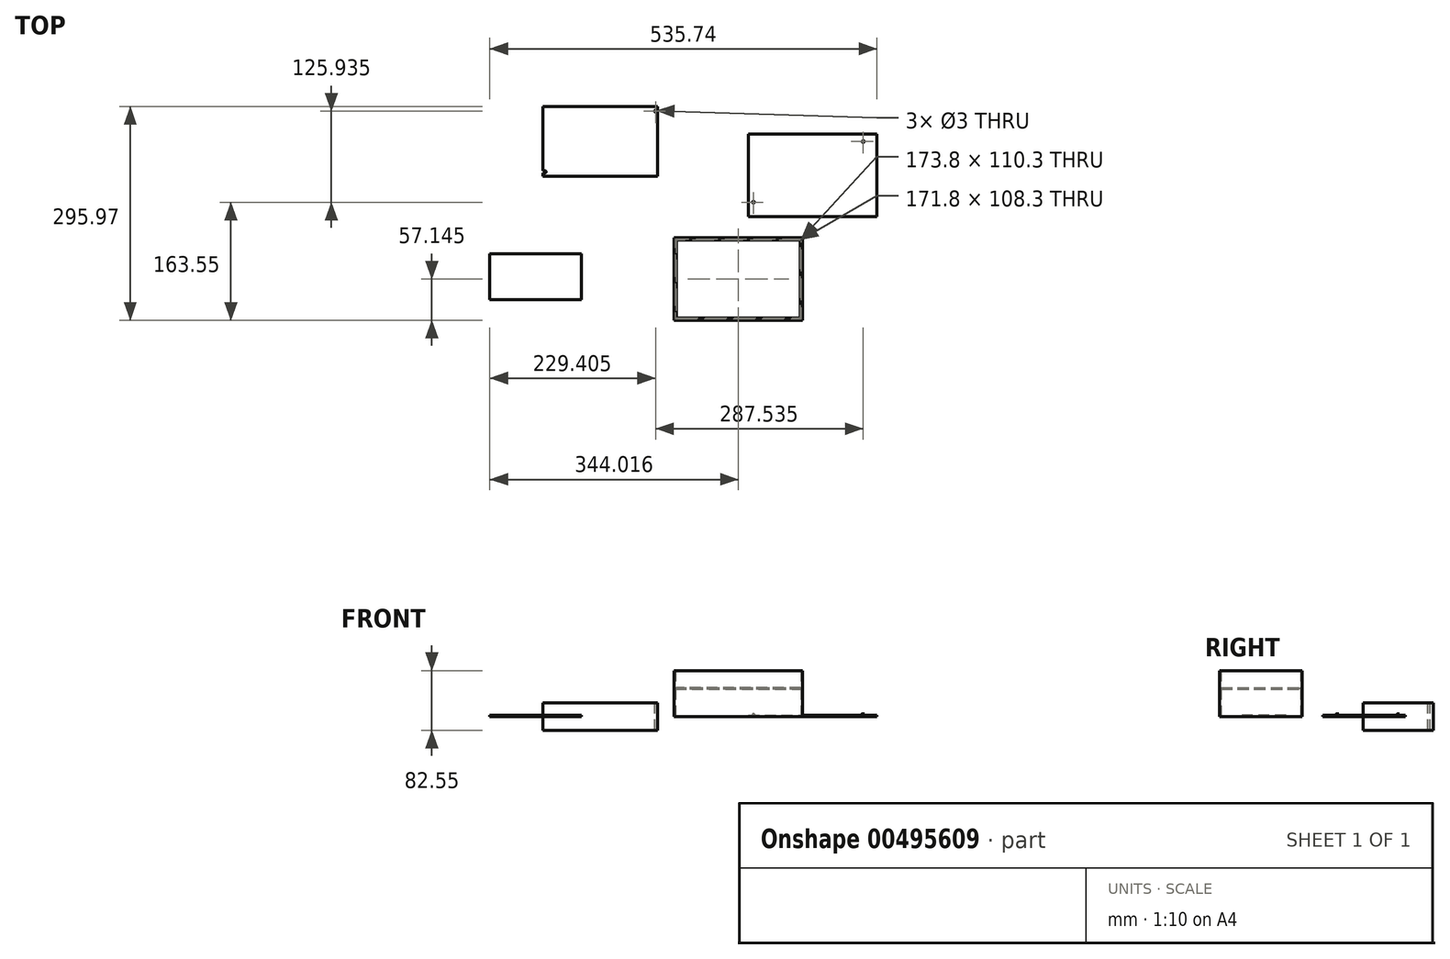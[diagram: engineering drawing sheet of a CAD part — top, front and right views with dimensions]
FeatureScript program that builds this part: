
annotation { "Feature Type Name" : "Feature", "Feature Type Description" : "" }
export const myFeature = defineFeature(function(context is Context, id is Id, definition is map)
    precondition{}
    {
        {
            var Q0;
            Q0=qCreatedBy(makeId("Top.planeOp"),FACE);
            var sketch = newSketch(context, id + "F0", { "sketchPlane" : qUnion([Q0])});
            skLineSegment(sketch, "E0.bottom", {"start": v(79.38, -48.42) * mm, "end": v(-79.38, -48.42) * mm});
            skLineSegment(sketch, "E0.top", {"start": v(79.38, 48.42) * mm, "end": v(-79.38, 48.42) * mm});
            skLineSegment(sketch, "E0.left", {"start": v(79.38, -48.42) * mm, "end": v(79.38, 48.42) * mm});
            skLineSegment(sketch, "E0.right", {"start": v(-79.38, -48.42) * mm, "end": v(-79.38, 48.42) * mm});
            skPoint(sketch, "E0.middle", {"position": v(0, 0) * mm});
            skLineSegment(sketch, "E1.bottom", {"start": v(-79.38, -43.42) * mm, "end": v(-73.38, -43.42) * mm});
            skLineSegment(sketch, "E1.top", {"start": v(-79.38, -40.42) * mm, "end": v(-73.38, -40.42) * mm});
            skLineSegment(sketch, "E1.left", {"start": v(-79.38, -43.42) * mm, "end": v(-79.38, -40.42) * mm});
            skLineSegment(sketch, "E1.right", {"start": v(-73.38, -43.42) * mm, "end": v(-73.38, -40.42) * mm});
            skLineSegment(sketch, "E2.bottom", {"start": v(79.38, 43.42) * mm, "end": v(73.38, 43.42) * mm});
            skLineSegment(sketch, "E2.top", {"start": v(79.38, 40.42) * mm, "end": v(73.38, 40.42) * mm});
            skLineSegment(sketch, "E2.left", {"start": v(79.38, 43.42) * mm, "end": v(79.38, 40.42) * mm});
            skLineSegment(sketch, "E2.right", {"start": v(73.38, 43.42) * mm, "end": v(73.38, 40.42) * mm});
            skCircle(sketch, "E3", {"center": v(76.38, 41.93) * mm, "radius": 1.5 * mm});
            skCircle(sketch, "E4", {"center": v(-76.38, -41.92) * mm, "radius": 1.5 * mm});
            skPoint(sketch, "E4.centerSnap0", {"position": v(-76.38, -40.42) * mm});
            skSolve(sketch);
        }
        {
            var Q0;
            {var subQ6=sQuery(id+"F0.wireOp",EDGE,"E0.bottom");Q0=makeQuery(id+"F0.imprint","IMPRINT",FACE,{"disambiguationData":[TD([[makeQuery(id+"F0.imprint","IMPRINT",EDGE,{"derivedFrom":subQ6}),-1.0]])]});}
            var Q1;
            {var subQ0=sQuery(id+"F0.wireOp",EDGE,"E1.right");Q1=makeQuery(id+"F0.imprint","IMPRINT",FACE,{"disambiguationData":[TD([[makeQuery(id+"F0.imprint","IMPRINT",EDGE,{"derivedFrom":subQ0}),1.0]])]});}
            var Q2;
            {var subQ0=sQuery(id+"F0.wireOp",EDGE,"E1.left");Q2=makeQuery(id+"F0.imprint","IMPRINT",FACE,{"disambiguationData":[TD([[makeQuery(id+"F0.imprint","IMPRINT",EDGE,{"derivedFrom":subQ0}),-1.0]])]});}
            var Q3;
            Q3=makeQuery(id+"F0.imprint","IMPRINT",FACE,{"disambiguationData":[TD([[makeQuery(id+"F0.imprint","IMPRINT",EDGE,{"derivedFrom":sQuery(id+"F0.wireOp",EDGE,"E2.top")}),-1.0]])]});
            extrude(context, id + "F1", {"entities" : qUnion([Q0, Q1, Q2, Q3]), "endBound" : BoundingType.SYMMETRIC, "depth" : 38.1 * mm});
        }
        {
            var Q0;
            Q0=qCreatedBy(makeId("Top.planeOp"),FACE);
            var sketch = newSketch(context, id + "F2", { "sketchPlane" : qUnion([Q0])});
            skLineSegment(sketch, "E5.bottom", {"start": v(204.91, 10) * mm, "end": v(382.71, 10) * mm});
            skLineSegment(sketch, "E5.top", {"start": v(204.91, -104.3) * mm, "end": v(382.71, -104.3) * mm});
            skLineSegment(sketch, "E5.left", {"start": v(204.91, 10) * mm, "end": v(204.91, -104.3) * mm});
            skLineSegment(sketch, "E5.right", {"start": v(382.71, 10) * mm, "end": v(382.71, -104.3) * mm});
            skCircle(sketch, "E6", {"center": v(363.91, 0) * mm, "radius": 1.5 * mm});
            skCircle(sketch, "E7", {"center": v(211.91, -84) * mm, "radius": 1.5 * mm});
            skSolve(sketch);
        }
        {
            var Q0;
            Q0=makeQuery(id+"F2.imprint","IMPRINT",FACE,{"disambiguationData":[TD([[makeQuery(id+"F2.imprint","IMPRINT",EDGE,{"derivedFrom":sQuery(id+"F2.wireOp",EDGE,"E7")}),1.0]])]});
            var Q1;
            Q1=makeQuery(id+"F2.imprint","IMPRINT",FACE,{"disambiguationData":[TD([[makeQuery(id+"F2.imprint","IMPRINT",EDGE,{"derivedFrom":sQuery(id+"F2.wireOp",EDGE,"E6")}),1.0]])]});
            extrude(context, id + "F3", {"entities" : qUnion([Q0, Q1]), "depth" : 4 * mm});
        }
        {
            var Q0;
            Q0=makeQuery(id+"F2.imprint","IMPRINT",FACE,{"disambiguationData":[TD([[makeQuery(id+"F2.imprint","IMPRINT",EDGE,{"derivedFrom":sQuery(id+"F2.wireOp",EDGE,"E5.bottom")}),-1.0]])]});
            extrude(context, id + "F4", {"entities" : qUnion([Q0]), "depth" : 2 * mm});
        }
        {
            var Q0;
            Q0=qCreatedBy(makeId("Top.planeOp"),FACE);
            var sketch = newSketch(context, id + "F5", { "sketchPlane" : qUnion([Q0])});
            skLineSegment(sketch, "E8.bottom", {"start": v(-153.03, -155.5) * mm, "end": v(-26.03, -155.5) * mm});
            skLineSegment(sketch, "E8.top", {"start": v(-153.03, -219) * mm, "end": v(-26.03, -219) * mm});
            skLineSegment(sketch, "E8.left", {"start": v(-153.03, -155.5) * mm, "end": v(-153.03, -219) * mm});
            skLineSegment(sketch, "E8.right", {"start": v(-26.03, -155.5) * mm, "end": v(-26.03, -219) * mm});
            skSolve(sketch);
        }
        {
            var Q0;
            Q0=qCreatedBy(makeId("Top.planeOp"),FACE);
            var sketch = newSketch(context, id + "F6", { "sketchPlane" : qUnion([Q0])});
            skLineSegment(sketch, "E9.bottom", {"start": v(102.09, -133.25) * mm, "end": v(279.89, -133.25) * mm});
            skLineSegment(sketch, "E9.top", {"start": v(102.09, -247.55) * mm, "end": v(279.89, -247.55) * mm});
            skLineSegment(sketch, "E9.left", {"start": v(102.09, -133.25) * mm, "end": v(102.09, -247.55) * mm});
            skLineSegment(sketch, "E9.right", {"start": v(279.89, -133.25) * mm, "end": v(279.89, -247.55) * mm});
            skLineSegment(sketch, "E10.bottom", {"start": v(104.09, -135.25) * mm, "end": v(277.89, -135.25) * mm});
            skLineSegment(sketch, "E10.top", {"start": v(104.09, -245.55) * mm, "end": v(277.89, -245.55) * mm});
            skLineSegment(sketch, "E10.left", {"start": v(104.09, -135.25) * mm, "end": v(104.09, -245.55) * mm});
            skLineSegment(sketch, "E10.right", {"start": v(277.89, -135.25) * mm, "end": v(277.89, -245.55) * mm});
            skSolve(sketch);
        }
        {
            var Q0;
            Q0=makeQuery(id+"F6.imprint","IMPRINT",FACE,{"disambiguationData":[TD([[makeQuery(id+"F6.imprint","IMPRINT",EDGE,{"derivedFrom":sQuery(id+"F6.wireOp",EDGE,"E9.bottom")}),-1.0]])]});
            extrude(context, id + "F7", {"entities" : qUnion([Q0]), "depth" : 63.5 * mm});
        }
        {
            var Q0;
            Q0=makeQuery(id+"F7.opExtrude","SWEPT_FACE",FACE,{"disambiguationData":[OSD([sQuery(id+"F6.wireOp",EDGE,"E10.top")])]});
            var sketch = newSketch(context, id + "F8", { "sketchPlane" : qUnion([Q0])});
            skLineSegment(sketch, "E11.bottom", {"start": v(-277.89, 38.1) * mm, "end": v(-104.09, 38.1) * mm});
            skLineSegment(sketch, "E11.top", {"start": v(-277.89, 40.1) * mm, "end": v(-104.09, 40.1) * mm});
            skLineSegment(sketch, "E11.left", {"start": v(-277.89, 38.1) * mm, "end": v(-277.89, 40.1) * mm});
            skLineSegment(sketch, "E11.right", {"start": v(-104.09, 38.1) * mm, "end": v(-104.09, 40.1) * mm});
            skLineSegment(sketch, "E12.bottom", {"start": v(-104.09, 38.1) * mm, "end": v(-104.09, 38.1) * mm});
            skLineSegment(sketch, "E12.top", {"start": v(-104.09, 40.1) * mm, "end": v(-104.09, 40.1) * mm});
            skSolve(sketch);
        }
        {
            var Q0;
            Q0=makeQuery(id+"F7.opExtrude","SWEPT_FACE",FACE,{"disambiguationData":[OSD([sQuery(id+"F6.wireOp",EDGE,"E10.left")])]});
            var sketch = newSketch(context, id + "F9", { "sketchPlane" : qUnion([Q0])});
            skLineSegment(sketch, "E13.bottom", {"start": v(-245.55, 38.1) * mm, "end": v(-135.25, 38.1) * mm});
            skLineSegment(sketch, "E13.top", {"start": v(-245.55, 40.1) * mm, "end": v(-135.25, 40.1) * mm});
            skLineSegment(sketch, "E13.left", {"start": v(-245.55, 38.1) * mm, "end": v(-245.55, 40.1) * mm});
            skLineSegment(sketch, "E13.right", {"start": v(-135.25, 38.1) * mm, "end": v(-135.25, 40.1) * mm});
            skSolve(sketch);
        }
        {
            var Q0;
            Q0=makeQuery(id+"F7.opExtrude","SWEPT_FACE",FACE,{"disambiguationData":[OSD([sQuery(id+"F6.wireOp",EDGE,"E10.bottom")])]});
            var sketch = newSketch(context, id + "F10", { "sketchPlane" : qUnion([Q0])});
            skLineSegment(sketch, "E14.bottom", {"start": v(104.09, 38.1) * mm, "end": v(277.89, 38.1) * mm});
            skLineSegment(sketch, "E14.top", {"start": v(104.09, 40.1) * mm, "end": v(277.89, 40.1) * mm});
            skLineSegment(sketch, "E14.left", {"start": v(104.09, 38.1) * mm, "end": v(104.09, 40.1) * mm});
            skLineSegment(sketch, "E14.right", {"start": v(277.89, 38.1) * mm, "end": v(277.89, 40.1) * mm});
            skSolve(sketch);
        }
        {
            var Q0;
            Q0=makeQuery(id+"F7.opExtrude","SWEPT_FACE",FACE,{"disambiguationData":[OSD([sQuery(id+"F6.wireOp",EDGE,"E10.right")])]});
            var sketch = newSketch(context, id + "F11", { "sketchPlane" : qUnion([Q0])});
            skLineSegment(sketch, "E15.bottom", {"start": v(135.25, 38.1) * mm, "end": v(245.55, 38.1) * mm});
            skLineSegment(sketch, "E15.top", {"start": v(135.25, 40.1) * mm, "end": v(245.55, 40.1) * mm});
            skLineSegment(sketch, "E15.left", {"start": v(135.25, 38.1) * mm, "end": v(135.25, 40.1) * mm});
            skLineSegment(sketch, "E15.right", {"start": v(245.55, 38.1) * mm, "end": v(245.55, 40.1) * mm});
            skSolve(sketch);
        }
        {
            var Q0;
            Q0=makeQuery(id+"F10.imprint","IMPRINT",FACE,{"disambiguationData":[TD([[makeQuery(id+"F10.imprint","IMPRINT",EDGE,{"derivedFrom":sQuery(id+"F10.wireOp",EDGE,"E14.bottom")}),1.0]])]});
            extrude(context, id + "F12", {"entities" : qUnion([Q0]), "operationType" : NewBodyOperationType.ADD, "depth" : 1 * mm});
        }
        {
            var Q0;
            Q0=makeQuery(id+"F11.imprint","IMPRINT",FACE,{"disambiguationData":[TD([[makeQuery(id+"F11.imprint","IMPRINT",EDGE,{"derivedFrom":sQuery(id+"F11.wireOp",EDGE,"E15.bottom")}),1.0]])]});
            extrude(context, id + "F13", {"entities" : qUnion([Q0]), "operationType" : NewBodyOperationType.ADD, "depth" : 1 * mm});
        }
        {
            var Q0;
            Q0=makeQuery(id+"F9.imprint","IMPRINT",FACE,{"disambiguationData":[TD([[makeQuery(id+"F9.imprint","IMPRINT",EDGE,{"derivedFrom":sQuery(id+"F9.wireOp",EDGE,"E13.bottom")}),1.0]])]});
            extrude(context, id + "F14", {"entities" : qUnion([Q0]), "operationType" : NewBodyOperationType.ADD, "depth" : 1 * mm});
        }
        {
            var Q0;
            Q0=makeQuery(id+"F8.imprint","IMPRINT",FACE,{"disambiguationData":[TD([[makeQuery(id+"F8.imprint","IMPRINT",EDGE,{"derivedFrom":sQuery(id+"F8.wireOp",EDGE,"E11.bottom")}),1.0]])]});
            extrude(context, id + "F15", {"entities" : qUnion([Q0]), "operationType" : NewBodyOperationType.ADD, "depth" : 1 * mm});
        }
        {
            var Q0;
            Q0=makeQuery(id+"F5.imprint","IMPRINT",FACE,{"disambiguationData":[TD([[makeQuery(id+"F5.imprint","IMPRINT",EDGE,{"derivedFrom":sQuery(id+"F5.wireOp",EDGE,"E8.bottom")}),-1.0]])]});
            extrude(context, id + "F16", {"entities" : qUnion([Q0]), "depth" : 2 * mm});
        }
    });
